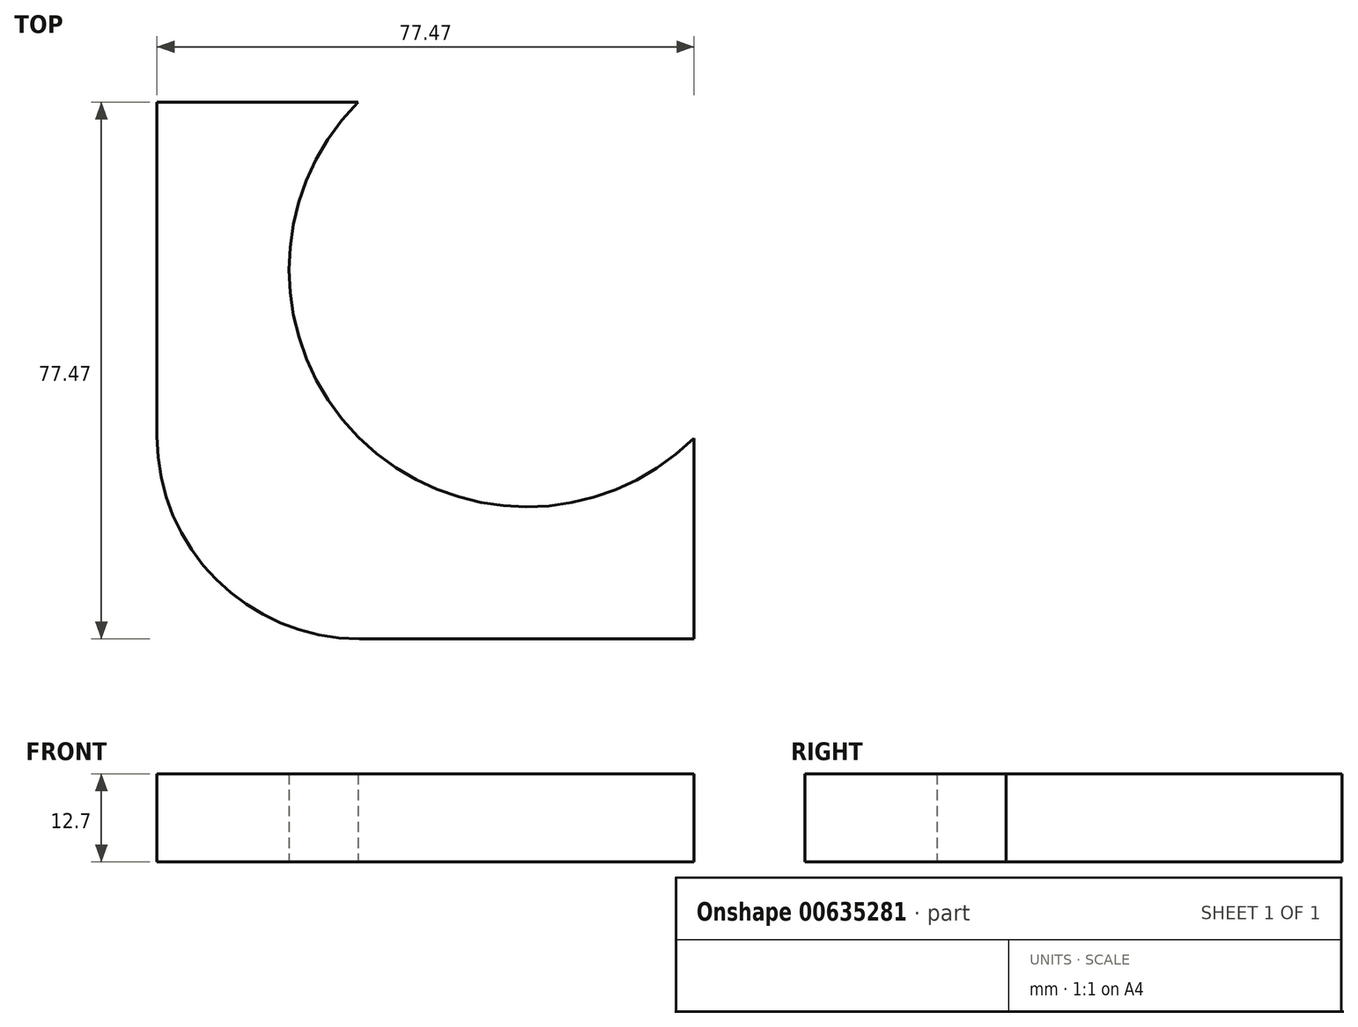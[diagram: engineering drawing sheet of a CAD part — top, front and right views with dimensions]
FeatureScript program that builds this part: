
annotation { "Feature Type Name" : "Feature", "Feature Type Description" : "" }
export const myFeature = defineFeature(function(context is Context, id is Id, definition is map)
    precondition{}
    {
        {
            var Q0;
            Q0=qCreatedBy(makeId("Top.planeOp"),FACE);
            var sketch = newSketch(context, id + "F0", { "sketchPlane" : qUnion([Q0])});
            skArc(sketch, "E0", {"start": v(-24.36, 24.13) * mm, "mid": v(-24.25, -24.25) * mm, "end": v(24.13, -24.36) * mm});
            skLineSegment(sketch, "E1", {"start": v(-53.34, 24.13) * mm, "end": v(-53.34, -24.13) * mm});
            skLineSegment(sketch, "E2", {"start": v(24.13, -53.34) * mm, "end": v(-24.13, -53.34) * mm});
            skLineSegment(sketch, "E3", {"start": v(-53.34, 24.13) * mm, "end": v(-24.36, 24.13) * mm});
            skLineSegment(sketch, "E4.trimOffspring", {"start": v(24.13, -24.36) * mm, "end": v(24.13, -53.34) * mm});
            skArc(sketch, "E5.filletArc", {"start": v(-53.34, -24.13) * mm, "mid": v(-44.78, -44.78) * mm, "end": v(-24.13, -53.34) * mm});
            skSolve(sketch);
        }
        {
            var Q0;
            Q0=makeQuery(id+"F0.imprint","IMPRINT",FACE,{"disambiguationData":[TD([[makeQuery(id+"F0.imprint","IMPRINT",EDGE,{"derivedFrom":sQuery(id+"F0.wireOp",EDGE,"E0")}),-1.0]])]});
            extrude(context, id + "F1", {"entities" : qUnion([Q0]), "depth" : 12.7 * mm, "offsetDistance" : 25.4 * mm});
        }
    });
